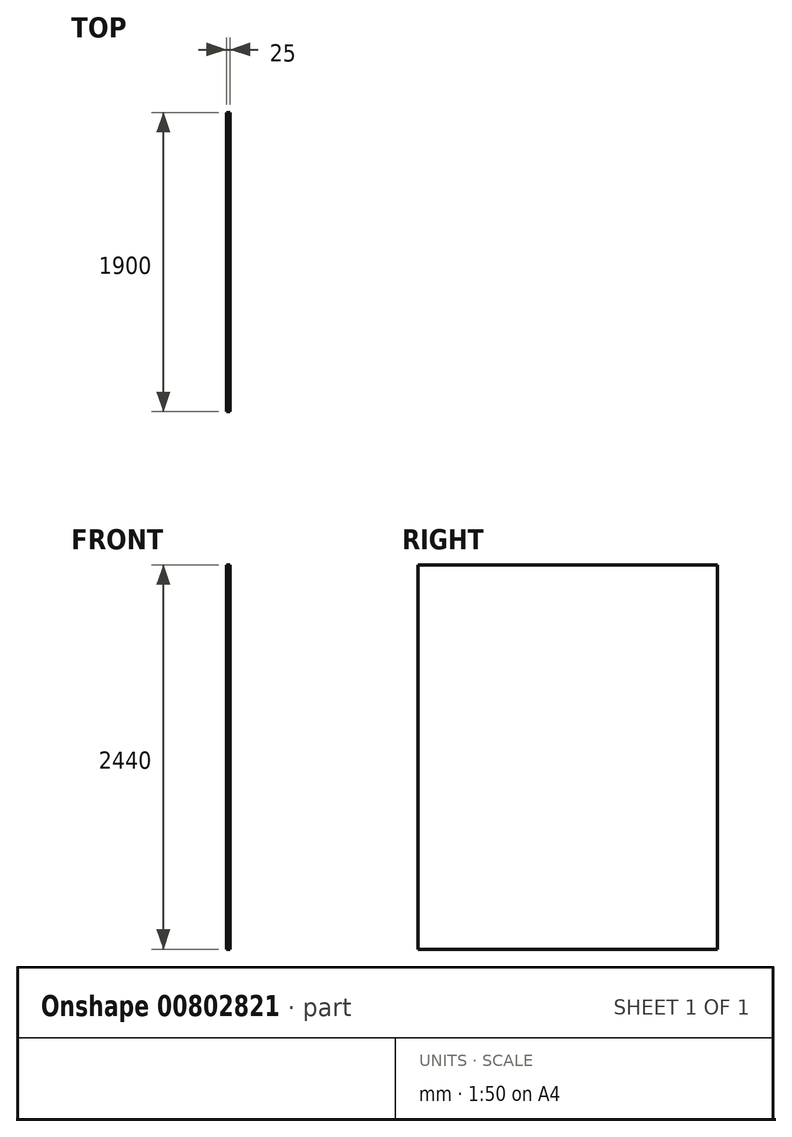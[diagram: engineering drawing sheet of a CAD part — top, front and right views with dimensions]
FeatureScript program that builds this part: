
annotation { "Feature Type Name" : "Feature", "Feature Type Description" : "" }
export const myFeature = defineFeature(function(context is Context, id is Id, definition is map)
    precondition{}
    {
        {
            var Q0;
            Q0=qCreatedBy(makeId("Right.planeOp"),FACE);
            var sketch = newSketch(context, id + "F0", { "sketchPlane" : qUnion([Q0])});
            skLineSegment(sketch, "E0.bottom", {"start": v(0, 0) * mm, "end": v(1900, 0) * mm});
            skLineSegment(sketch, "E0.top", {"start": v(0, 2440) * mm, "end": v(1900, 2440) * mm});
            skLineSegment(sketch, "E0.left", {"start": v(0, 0) * mm, "end": v(0, 2440) * mm});
            skLineSegment(sketch, "E0.right", {"start": v(1900, 0) * mm, "end": v(1900, 2440) * mm});
            skSolve(sketch);
        }
        {
            var Q0;
            Q0 = qSketchRegion(id + "F0", true);
            extrude(context, id + "F1", {"entities" : qUnion([Q0]), "depth" : 25 * mm, "offsetDistance" : 25 * mm});
        }
    });
